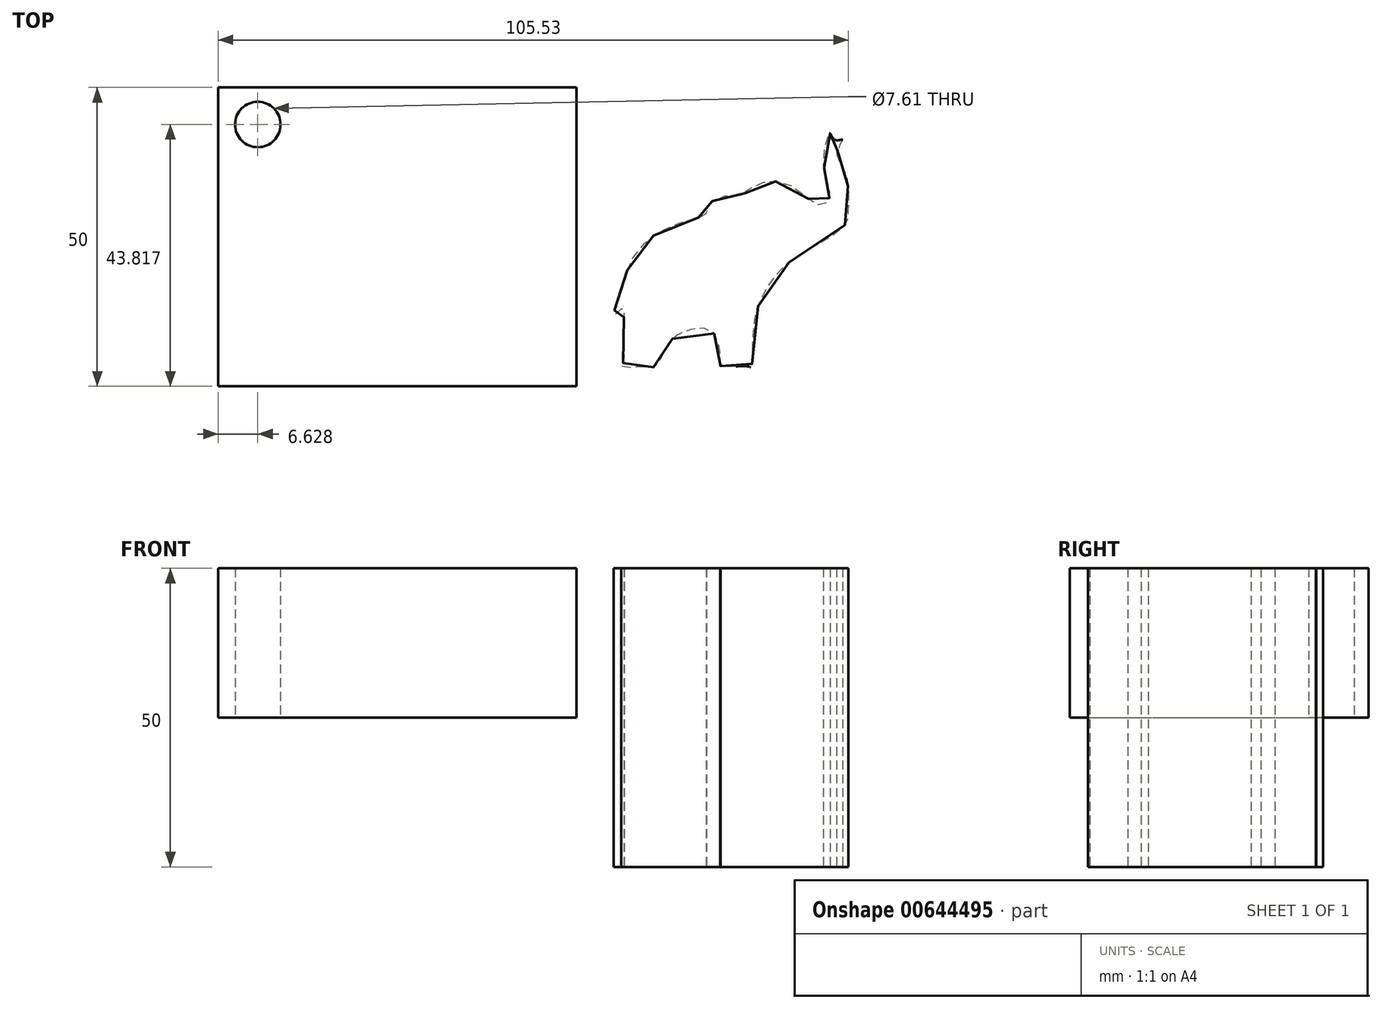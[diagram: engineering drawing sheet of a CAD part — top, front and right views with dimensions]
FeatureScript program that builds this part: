
annotation { "Feature Type Name" : "Feature", "Feature Type Description" : "" }
export const myFeature = defineFeature(function(context is Context, id is Id, definition is map)
    precondition{}
    {
        {
            var Q0;
            Q0=qCreatedBy(makeId("Top.planeOp"),FACE);
            var sketch = newSketch(context, id + "F0", { "sketchPlane" : qUnion([Q0])});
            skLineSegment(sketch, "E0.bottom", {"start": v(0, 0) * mm, "end": v(-60, 0) * mm});
            skLineSegment(sketch, "E0.top", {"start": v(0, 50) * mm, "end": v(-60, 50) * mm});
            skLineSegment(sketch, "E0.left", {"start": v(0, 0) * mm, "end": v(0, 50) * mm});
            skLineSegment(sketch, "E0.right", {"start": v(-60, 0) * mm, "end": v(-60, 50) * mm});
            skCircle(sketch, "E1", {"center": v(-53.37, 43.82) * mm, "radius": 3.8 * mm});
            skFitSpline(sketch, "E2", {"points": [v(6.33, 12.69) * mm, v(7.66, 16.48) * mm, v(8.83, 20.31) * mm, v(11.45, 23.97) * mm, v(15.21, 26.52) * mm, v(20.52, 28.24) * mm, v(21.76, 28.67) * mm, v(21.7, 29.34) * mm, v(22.33, 30.65) * mm, v(25.7, 32) * mm, v(28.04, 32.07) * mm, v(28.51, 32.74) * mm, v(31.57, 34.21) * mm, v(33.72, 34.21) * mm, v(36.3, 33.4) * mm, v(39.4, 30.92) * mm, v(40.8, 30.32) * mm, v(41.98, 30.72) * mm, v(42.45, 32) * mm, v(42.18, 33.64) * mm, v(41.54, 36.3) * mm, v(41.38, 38.85) * mm, v(42.34, 42.38) * mm, v(43.3, 41.25) * mm, v(44.58, 41.25) * mm, v(43.62, 39.33) * mm, v(44.74, 36.3) * mm, v(45.48, 33.36) * mm, v(45.48, 29.18) * mm, v(44.59, 26.56) * mm, v(35.32, 20.51) * mm, v(31.09, 14.94) * mm, v(29.6, 9.9) * mm, v(29.34, 3.05) * mm, v(28.94, 3.25) * mm, v(24.23, 3.32) * mm, v(24.1, 3.92) * mm, v(23.83, 6.88) * mm, v(22.15, 9.5) * mm, v(17.05, 8.7) * mm, v(14.7, 5.87) * mm, v(13.22, 3.25) * mm, v(12.21, 3.25) * mm, v(7.5, 3.25) * mm, v(7.84, 3.85) * mm, v(7.98, 5.26) * mm, v(7.98, 12.18) * mm, v(7.78, 13.12) * mm, v(6.33, 11.91) * mm, v(6.33, 12.69) * mm]});
            skSolve(sketch);
        }
        {
            var Q0;
            Q0=makeQuery(id+"F0.imprint","IMPRINT",FACE,{"disambiguationData":[TD([[makeQuery(id+"F0.imprint","IMPRINT",EDGE,{"derivedFrom":sQuery(id+"F0.wireOp",EDGE,"E0.bottom")}),-1.0]])]});
            extrude(context, id + "F1", {"entities" : qUnion([Q0]), "depth" : 3 * mm, "offsetDistance" : 25 * mm});
        }
        {
            var Q0;
            Q0 = qSketchRegion(id + "F0", true);
            extrude(context, id + "F2", {"entities" : qUnion([Q0]), "operationType" : NewBodyOperationType.ADD, "depth" : 25 * mm, "offsetDistance" : 25 * mm});
        }
        {
            var Q0;
            Q0=makeQuery(id+"F2.opExtrude","CAP_FACE",FACE,{"disambiguationData":[OSD([sQuery(id+"F0.wireOp",EDGE,"E2")])],"isStart":true});
            var Q1;
            Q1=makeQuery(id+"F2.opExtrude","CAP_FACE",FACE,{"disambiguationData":[OSD([sQuery(id+"F0.wireOp",EDGE,"E2")])],"isStart":false});
            extrude(context, id + "F3", {"entities" : qUnion([Q0, Q1]), "operationType" : NewBodyOperationType.ADD, "depth" : 25 * mm, "offsetDistance" : 25 * mm});
        }
    });
